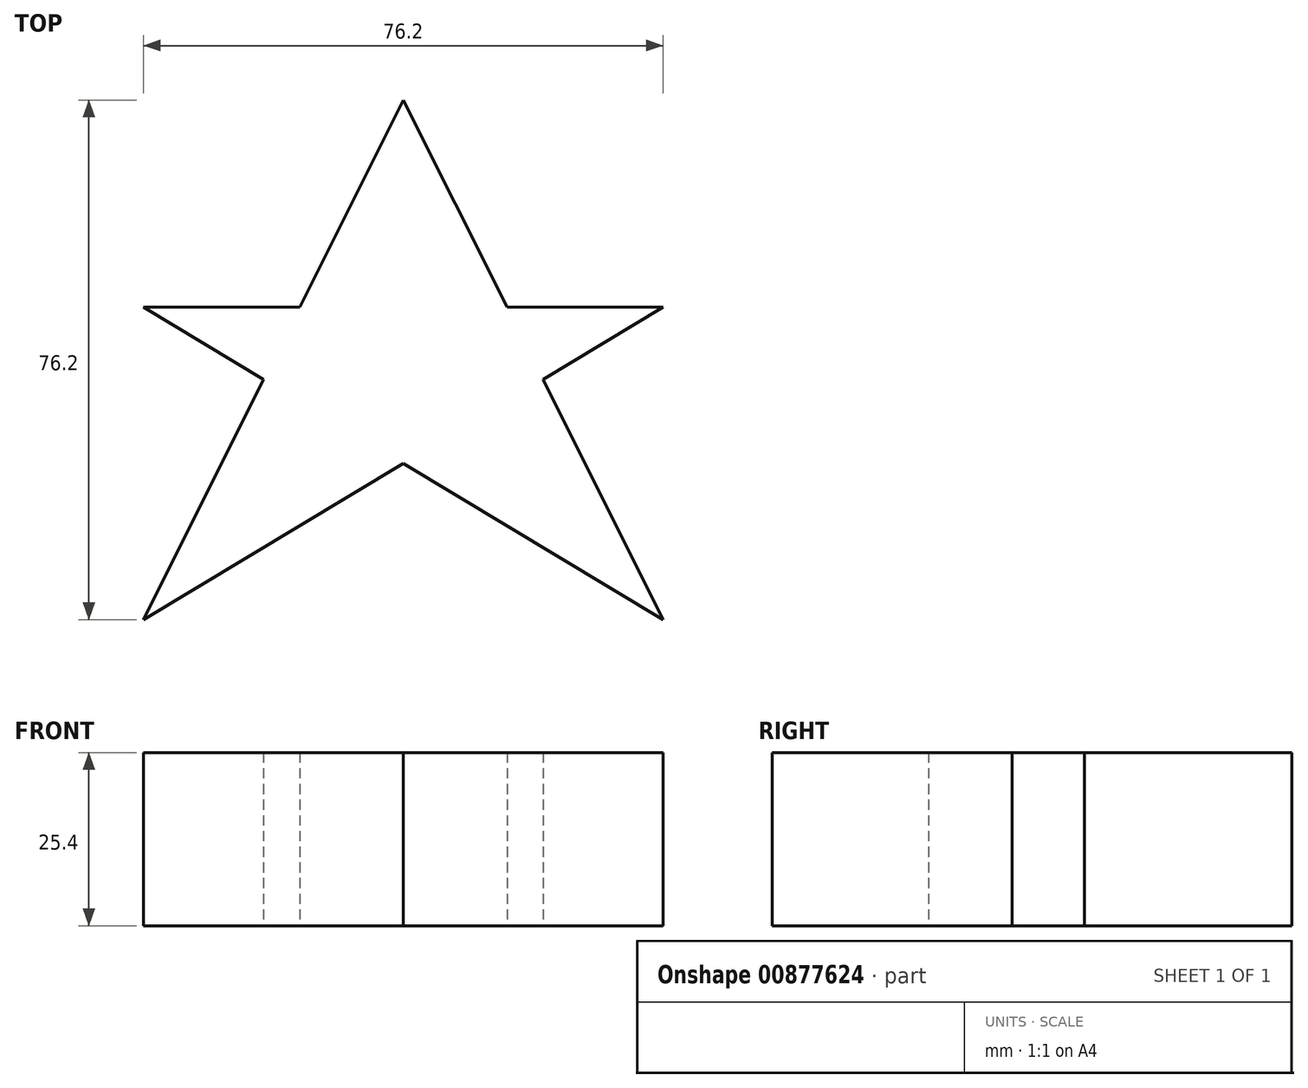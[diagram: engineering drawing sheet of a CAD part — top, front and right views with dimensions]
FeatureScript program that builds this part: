
annotation { "Feature Type Name" : "Feature", "Feature Type Description" : "" }
export const myFeature = defineFeature(function(context is Context, id is Id, definition is map)
    precondition{}
    {
        {
            var Q0;
            Q0=qCreatedBy(makeId("Top.planeOp"),FACE);
            var sketch = newSketch(context, id + "F0", { "sketchPlane" : qUnion([Q0])});
            skLineSegment(sketch, "E0.bottom", {"start": v(0, 0) * mm, "end": v(76.2, 0) * mm});
            skLineSegment(sketch, "E0.top", {"start": v(0, 76.2) * mm, "end": v(76.2, 76.2) * mm});
            skLineSegment(sketch, "E0.left", {"start": v(0, 0) * mm, "end": v(0, 76.2) * mm});
            skLineSegment(sketch, "E0.right", {"start": v(76.2, 0) * mm, "end": v(76.2, 76.2) * mm});
            skLineSegment(sketch, "E1", {"start": v(0, 0) * mm, "end": v(76.2, 45.79) * mm});
            skLineSegment(sketch, "E2", {"start": v(76.2, 45.79) * mm, "end": v(0, 45.79) * mm});
            skLineSegment(sketch, "E3", {"start": v(0, 45.79) * mm, "end": v(76.2, 0) * mm});
            skLineSegment(sketch, "E4", {"start": v(76.2, 0) * mm, "end": v(38.1, 76.2) * mm});
            skLineSegment(sketch, "E5", {"start": v(38.1, 76.2) * mm, "end": v(0, 0) * mm});
            skSolve(sketch);
        }
        {
            var Q0;
            {var subQ0=sQuery(id+"F0.wireOp",EDGE,"E4");var subQ1=sQuery(id+"F0.wireOp",EDGE,"E2");var subQ2=makeQuery(id+"F0.imprint","INTERSECT",VERTEX,{"derivedFrom":[subQ1,subQ0]});Q0=makeQuery(id+"F0.imprint","IMPRINT",FACE,{"disambiguationData":[TD([[makeQuery(id+"F0.imprint","IMPRINT",EDGE,{"disambiguationData":[TD([[subQ2,-1.0]])],"derivedFrom":subQ1}),-1.0]])]});}
            var Q1;
            {var subQ1=sQuery(id+"F0.wireOp",EDGE,"E2");var subQ3=sQuery(id+"F0.wireOp",EDGE,"E5");var subQ4=makeQuery(id+"F0.imprint","INTERSECT",VERTEX,{"derivedFrom":[subQ1,subQ3]});Q1=makeQuery(id+"F0.imprint","IMPRINT",FACE,{"disambiguationData":[TD([[makeQuery(id+"F0.imprint","IMPRINT",EDGE,{"disambiguationData":[TD([[subQ4,-1.0]])],"derivedFrom":subQ3}),-1.0]])]});}
            var Q2;
            {var subQ1=sQuery(id+"F0.wireOp",EDGE,"E1");var subQ3=sQuery(id+"F0.wireOp",EDGE,"E3");var subQ4=makeQuery(id+"F0.imprint","INTERSECT",VERTEX,{"derivedFrom":[subQ1,subQ3]});Q2=makeQuery(id+"F0.imprint","IMPRINT",FACE,{"disambiguationData":[TD([[makeQuery(id+"F0.imprint","IMPRINT",EDGE,{"disambiguationData":[TD([[subQ4,1.0]])],"derivedFrom":subQ3}),-1.0]])]});}
            var Q3;
            {var subQ0=sQuery(id+"F0.wireOp",EDGE,"E3");var subQ1=sQuery(id+"F0.wireOp",EDGE,"E1");var subQ2=makeQuery(id+"F0.imprint","INTERSECT",VERTEX,{"derivedFrom":[subQ1,subQ0]});Q3=makeQuery(id+"F0.imprint","IMPRINT",FACE,{"disambiguationData":[TD([[makeQuery(id+"F0.imprint","IMPRINT",EDGE,{"disambiguationData":[TD([[subQ2,-1.0]])],"derivedFrom":subQ1}),-1.0]])]});}
            var Q4;
            {var subQ1=sQuery(id+"F0.wireOp",EDGE,"E1");var subQ3=sQuery(id+"F0.wireOp",EDGE,"E4");var subQ4=makeQuery(id+"F0.imprint","INTERSECT",VERTEX,{"derivedFrom":[subQ1,subQ3]});Q4=makeQuery(id+"F0.imprint","IMPRINT",FACE,{"disambiguationData":[TD([[makeQuery(id+"F0.imprint","IMPRINT",EDGE,{"disambiguationData":[TD([[subQ4,-1.0]])],"derivedFrom":subQ3}),-1.0]])]});}
            var Q5;
            {var subQ1=sQuery(id+"F0.wireOp",EDGE,"E1");var subQ5=sQuery(id+"F0.wireOp",EDGE,"E3");var subQ6=makeQuery(id+"F0.imprint","INTERSECT",VERTEX,{"derivedFrom":[subQ1,subQ5]});Q5=makeQuery(id+"F0.imprint","IMPRINT",FACE,{"disambiguationData":[TD([[makeQuery(id+"F0.imprint","IMPRINT",EDGE,{"disambiguationData":[TD([[subQ6,-1.0]])],"derivedFrom":subQ1}),1.0]])]});}
            extrude(context, id + "F1", {"entities" : qUnion([Q0, Q1, Q2, Q3, Q4, Q5]), "depth" : 25.4 * mm, "offsetDistance" : 25.4 * mm});
        }
    });
